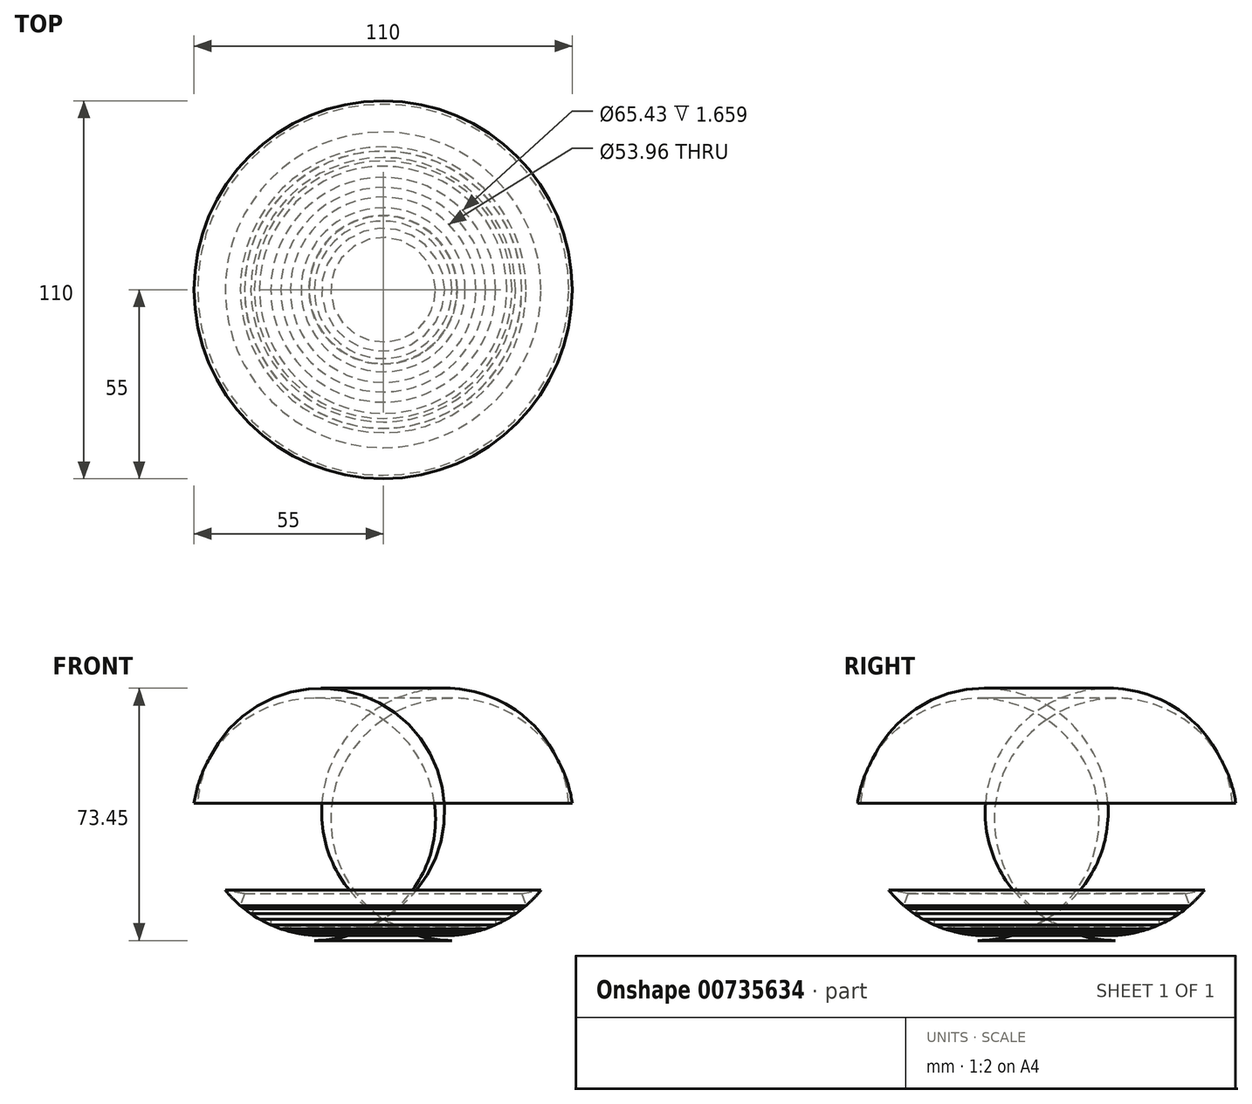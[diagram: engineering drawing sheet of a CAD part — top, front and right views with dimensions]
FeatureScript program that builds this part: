
annotation { "Feature Type Name" : "Feature", "Feature Type Description" : "" }
export const myFeature = defineFeature(function(context is Context, id is Id, definition is map)
    precondition{}
    {
        {
            var Q0;
            Q0=qCreatedBy(makeId("Front.planeOp"),FACE);
            var sketch = newSketch(context, id + "F0", { "sketchPlane" : qUnion([Q0])});
            skArc(sketch, "E0", {"start": v(-55, 40) * mm, "mid": v(-46.59, 12.05) * mm, "end": v(-20, 0) * mm});
            skLineSegment(sketch, "E1", {"start": v(-55, 40) * mm, "end": v(-54, 40) * mm});
            skLineSegment(sketch, "E2", {"start": v(-20, 0) * mm, "end": v(0, 0) * mm});
            skLineSegment(sketch, "E3", {"start": v(0, 0) * mm, "end": v(0, 3) * mm});
            skLineSegment(sketch, "E4", {"start": v(-20, 0) * mm, "end": v(-20, 1.5) * mm});
            skArc(sketch, "E5", {"start": v(-54, 40) * mm, "mid": v(-45.07, 13.62) * mm, "end": v(-20, 1.5) * mm});
            skLineSegment(sketch, "E6", {"start": v(-20, 1.5) * mm, "end": v(0, 3) * mm});
            skLineSegment(sketch, "E7", {"start": v(-21.47, 1.6) * mm, "end": v(-21.64, 3.85) * mm});
            skLineSegment(sketch, "E8", {"start": v(-21.64, 3.85) * mm, "end": v(-23.87, 1.92) * mm});
            skLineSegment(sketch, "E9", {"start": v(-26.98, 2.56) * mm, "end": v(-26.98, 4.23) * mm});
            skLineSegment(sketch, "E10", {"start": v(-26.98, 4.23) * mm, "end": v(-29.78, 3.4) * mm});
            skLineSegment(sketch, "E11", {"start": v(-32.72, 4.55) * mm, "end": v(-32.72, 6.21) * mm});
            skLineSegment(sketch, "E12", {"start": v(-32.72, 6.21) * mm, "end": v(-35.99, 6.21) * mm});
            skLineSegment(sketch, "E13", {"start": v(-38.5, 7.79) * mm, "end": v(-37.48, 9.16) * mm});
            skLineSegment(sketch, "E14", {"start": v(-37.48, 9.16) * mm, "end": v(-40.36, 9.16) * mm});
            skLineSegment(sketch, "E15", {"start": v(-41.58, 10.17) * mm, "end": v(-40.3, 13.62) * mm});
            skPoint(sketch, "E15.endSnap0", {"position": v(-45.07, 13.62) * mm});
            skLineSegment(sketch, "E16", {"start": v(-40.3, 13.62) * mm, "end": v(-45.94, 14.64) * mm});
            skSolve(sketch);
        }
        {
            var Q0;
            {var subQ0=sQuery(id+"F0.wireOp",EDGE,"E15");Q0=makeQuery(id+"F0.imprint","IMPRINT",FACE,{"disambiguationData":[TD([[makeQuery(id+"F0.imprint","IMPRINT",EDGE,{"derivedFrom":subQ0}),1.0]])]});}
            var Q1;
            {var subQ0=sQuery(id+"F0.wireOp",EDGE,"E13");Q1=makeQuery(id+"F0.imprint","IMPRINT",FACE,{"disambiguationData":[TD([[makeQuery(id+"F0.imprint","IMPRINT",EDGE,{"derivedFrom":subQ0}),1.0]])]});}
            var Q2;
            {var subQ0=sQuery(id+"F0.wireOp",EDGE,"E11");Q2=makeQuery(id+"F0.imprint","IMPRINT",FACE,{"disambiguationData":[TD([[makeQuery(id+"F0.imprint","IMPRINT",EDGE,{"derivedFrom":subQ0}),1.0]])]});}
            var Q3;
            {var subQ0=sQuery(id+"F0.wireOp",EDGE,"E9");Q3=makeQuery(id+"F0.imprint","IMPRINT",FACE,{"disambiguationData":[TD([[makeQuery(id+"F0.imprint","IMPRINT",EDGE,{"derivedFrom":subQ0}),1.0]])]});}
            var Q4;
            {var subQ0=sQuery(id+"F0.wireOp",EDGE,"E7");Q4=makeQuery(id+"F0.imprint","IMPRINT",FACE,{"disambiguationData":[TD([[makeQuery(id+"F0.imprint","IMPRINT",EDGE,{"derivedFrom":subQ0}),1.0]])]});}
            var Q5;
            Q5=makeQuery(id+"F0.imprint","IMPRINT",FACE,{"disambiguationData":[TD([[makeQuery(id+"F0.imprint","IMPRINT",EDGE,{"derivedFrom":sQuery(id+"F0.wireOp",EDGE,"E0")}),1.0]])]});
            var Q6;
            Q6=makeQuery(id+"F0.imprint","IMPRINT",FACE,{"disambiguationData":[TD([[makeQuery(id+"F0.imprint","IMPRINT",EDGE,{"derivedFrom":sQuery(id+"F0.wireOp",EDGE,"E2")}),1.0]])]});
            var Q7;
            Q7=sQuery(id+"F0.wireOp",EDGE,"E3");
            revolve(context, id + "F1", {"surfaceOperationType" : NewSurfaceOperationType.NEW, "entities" : qUnion([Q0, Q1, Q2, Q3, Q4, Q5, Q6]), "axis" : qUnion([Q7]), "revolveType" : RevolveType.FULL});
        }
    });
